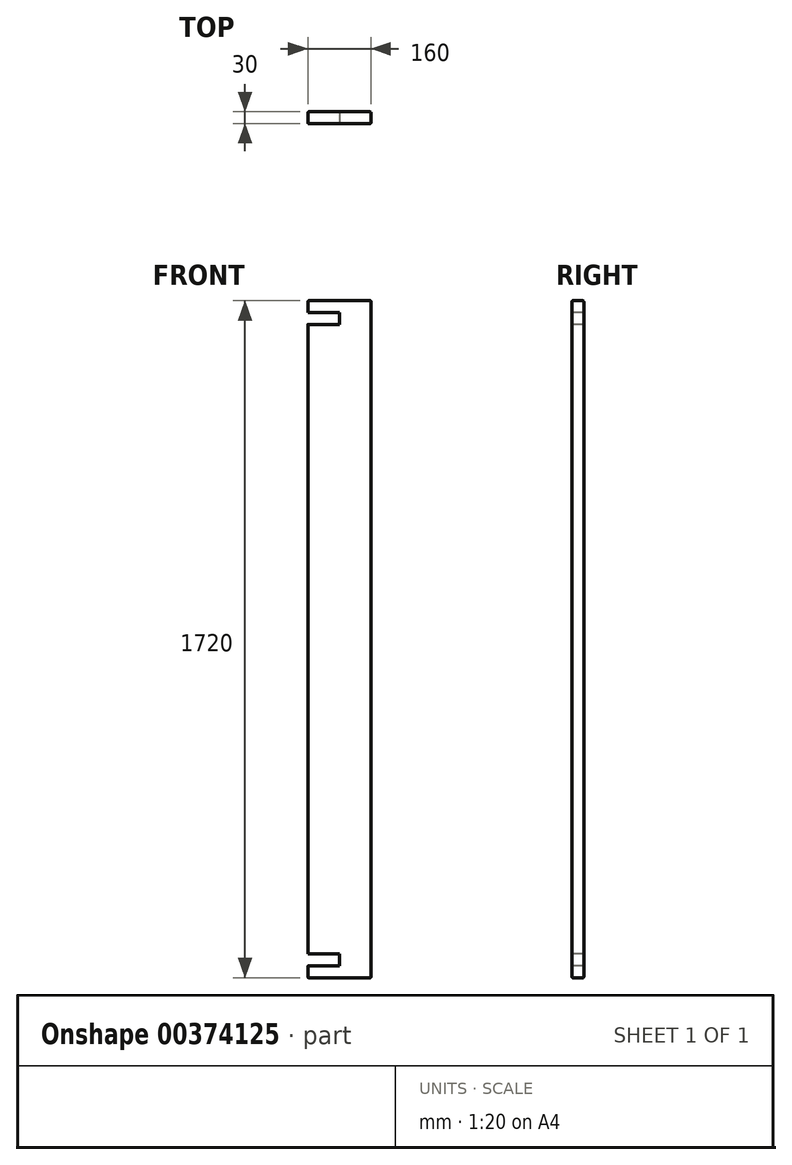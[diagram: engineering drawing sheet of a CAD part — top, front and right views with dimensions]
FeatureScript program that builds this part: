
annotation { "Feature Type Name" : "Feature", "Feature Type Description" : "" }
export const myFeature = defineFeature(function(context is Context, id is Id, definition is map)
    precondition{}
    {
        {
            var Q0;
            Q0=qCreatedBy(makeId("Top.planeOp"),FACE);
            var sketch = newSketch(context, id + "F0", { "sketchPlane" : qUnion([Q0])});
            skLineSegment(sketch, "E0.bottom", {"start": v(80, -15) * mm, "end": v(-80, -15) * mm});
            skLineSegment(sketch, "E0.top", {"start": v(80, 15) * mm, "end": v(-80, 15) * mm});
            skLineSegment(sketch, "E0.left", {"start": v(80, -15) * mm, "end": v(80, 15) * mm});
            skLineSegment(sketch, "E0.right", {"start": v(-80, -15) * mm, "end": v(-80, 15) * mm});
            skPoint(sketch, "E0.middle", {"position": v(0, 0) * mm});
            skSolve(sketch);
        }
        {
            var Q0;
            Q0 = qSketchRegion(id + "F0", true);
            extrude(context, id + "F1", {"entities" : qUnion([Q0]), "depth" : 1720 * mm, "symmetric" : true});
        }
        {
            var Q0;
            Q0=makeQuery(id+"F1.opExtrude","SWEPT_FACE",FACE,{"disambiguationData":[OSD([sQuery(id+"F0.wireOp",EDGE,"E0.bottom")])]});
            var Q1;
            Q1=makeQuery(id+"F1.opExtrude","SWEPT_FACE",FACE,{"disambiguationData":[OSD([sQuery(id+"F0.wireOp",EDGE,"E0.left")])]});
            var Q2;
            Q2=makeQuery(id+"F1.opExtrude","CAP_FACE",FACE,{"disambiguationData":[OSD([sQuery(id+"F0.wireOp",EDGE,"E0.bottom"),sQuery(id+"F0.wireOp",EDGE,"E0.top"),sQuery(id+"F0.wireOp",EDGE,"E0.left"),sQuery(id+"F0.wireOp",EDGE,"E0.right")])],"isStart":false});
            var Q3;
            Q3=makeQuery(id+"F1.opExtrude","SWEPT_FACE",FACE,{"disambiguationData":[OSD([sQuery(id+"F0.wireOp",EDGE,"E0.top")])]});
            var Q4;
            Q4=makeQuery(id+"F1.opExtrude","SWEPT_FACE",FACE,{"disambiguationData":[OSD([sQuery(id+"F0.wireOp",EDGE,"E0.right")])]});
            var Q5;
            Q5=makeQuery(id+"F1.opExtrude","CAP_FACE",FACE,{"disambiguationData":[OSD([sQuery(id+"F0.wireOp",EDGE,"E0.bottom"),sQuery(id+"F0.wireOp",EDGE,"E0.top"),sQuery(id+"F0.wireOp",EDGE,"E0.left"),sQuery(id+"F0.wireOp",EDGE,"E0.right")])],"isStart":true});
            fillet(context, id + "F2", {"entities" : qUnion([Q0, Q1, Q2, Q3, Q4, Q5]), "radius" : 2 * mm, "tangentPropagation" : true, "allowEdgeOverflow" : false});
        }
        {
            var Q0;
            Q0=makeQuery(id+"F1.opExtrude","SWEPT_FACE",FACE,{"disambiguationData":[OSD([sQuery(id+"F0.wireOp",EDGE,"E0.bottom")])]});
            var sketch = newSketch(context, id + "F3", { "sketchPlane" : qUnion([Q0])});
            skLineSegment(sketch, "E1.bottom", {"start": v(0, -830) * mm, "end": v(-80, -830) * mm});
            skLineSegment(sketch, "E1.top", {"start": v(0, -800) * mm, "end": v(-80, -800) * mm});
            skLineSegment(sketch, "E1.left", {"start": v(0, -830) * mm, "end": v(0, -800) * mm});
            skLineSegment(sketch, "E1.right", {"start": v(-80, -830) * mm, "end": v(-80, -800) * mm});
            skLineSegment(sketch, "E2", {"start": v(-78, 0) * mm, "end": v(78, 0) * mm, "construction": true});
            skLineSegment(sketch, "E3.MirrorCS", {"start": v(0, 830) * mm, "end": v(-80, 830) * mm});
            skLineSegment(sketch, "E4.MirrorCS", {"start": v(-80, 830) * mm, "end": v(-80, 800) * mm});
            skLineSegment(sketch, "E5.MirrorCS", {"start": v(0, 800) * mm, "end": v(-80, 800) * mm});
            skLineSegment(sketch, "E6.MirrorCS", {"start": v(0, 830) * mm, "end": v(0, 800) * mm});
            skSolve(sketch);
        }
        {
            var Q0;
            {var subQ0=sQuery(id+"F3.wireOp",EDGE,"E1.right");Q0=makeQuery(id+"F3.imprint","IMPRINT",FACE,{"disambiguationData":[TD([[makeQuery(id+"F3.imprint","IMPRINT",EDGE,{"derivedFrom":subQ0}),-1.0]])]});}
            var Q1;
            {var subQ0=sQuery(id+"F3.wireOp",EDGE,"E1.left");Q1=makeQuery(id+"F3.imprint","IMPRINT",FACE,{"disambiguationData":[TD([[makeQuery(id+"F3.imprint","IMPRINT",EDGE,{"derivedFrom":subQ0}),1.0]])]});}
            var Q2;
            {var subQ0=sQuery(id+"F3.wireOp",EDGE,"E4.MirrorCS");Q2=makeQuery(id+"F3.imprint","IMPRINT",FACE,{"disambiguationData":[TD([[makeQuery(id+"F3.imprint","IMPRINT",EDGE,{"derivedFrom":subQ0}),1.0]])]});}
            var Q3;
            {var subQ0=sQuery(id+"F3.wireOp",EDGE,"E6.MirrorCS");Q3=makeQuery(id+"F3.imprint","IMPRINT",FACE,{"disambiguationData":[TD([[makeQuery(id+"F3.imprint","IMPRINT",EDGE,{"derivedFrom":subQ0}),-1.0]])]});}
            extrude(context, id + "F4", {"entities" : qUnion([Q0, Q1, Q2, Q3]), "operationType" : NewBodyOperationType.REMOVE, "endBound" : BoundingType.THROUGH_ALL, "oppositeDirection" : true, "depth" : 25 * mm});
        }
    });
